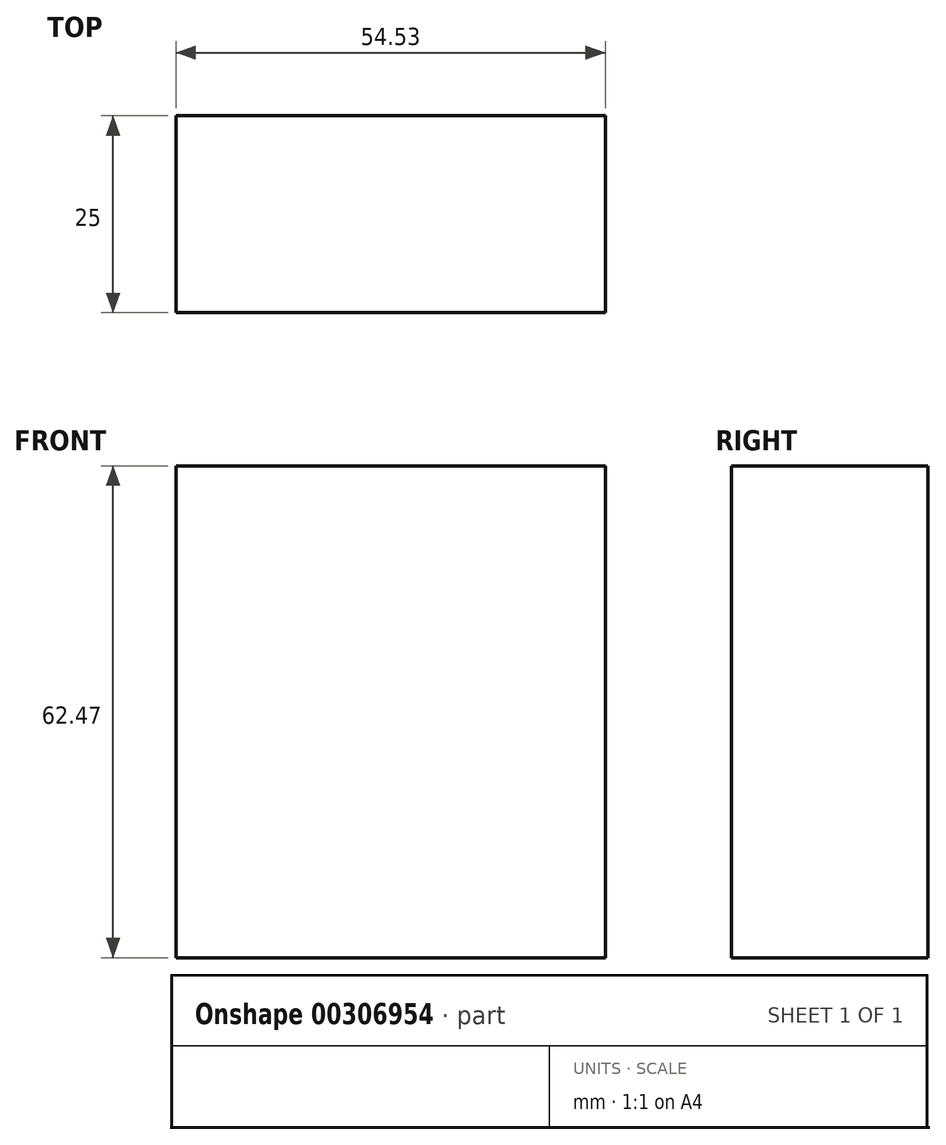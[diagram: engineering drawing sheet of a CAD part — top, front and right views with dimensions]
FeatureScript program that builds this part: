
annotation { "Feature Type Name" : "Feature", "Feature Type Description" : "" }
export const myFeature = defineFeature(function(context is Context, id is Id, definition is map)
    precondition{}
    {
        {
            var Q0;
            Q0=qCreatedBy(makeId("Front.planeOp"),FACE);
            var sketch = newSketch(context, id + "F0", { "sketchPlane" : qUnion([Q0])});
            skLineSegment(sketch, "E0.bottom", {"start": v(-99, 3.56) * mm, "end": v(-44.46, 3.56) * mm});
            skLineSegment(sketch, "E0.top", {"start": v(-99, 66.03) * mm, "end": v(-44.46, 66.03) * mm});
            skLineSegment(sketch, "E0.left", {"start": v(-99, 3.56) * mm, "end": v(-99, 66.03) * mm});
            skLineSegment(sketch, "E0.right", {"start": v(-44.46, 3.56) * mm, "end": v(-44.46, 66.03) * mm});
            skPoint(sketch, "E0.middle", {"position": v(-71.73, 34.8) * mm});
            skSolve(sketch);
        }
        {
            var Q0;
            Q0=makeQuery(id+"F0.imprint","IMPRINT",FACE,{"disambiguationData":[TD([[makeQuery(id+"F0.imprint","IMPRINT",EDGE,{"derivedFrom":sQuery(id+"F0.wireOp",EDGE,"E0.bottom")}),1.0]])]});
            extrude(context, id + "F1", {"entities" : qUnion([Q0]), "depth" : 25 * mm});
        }
    });
